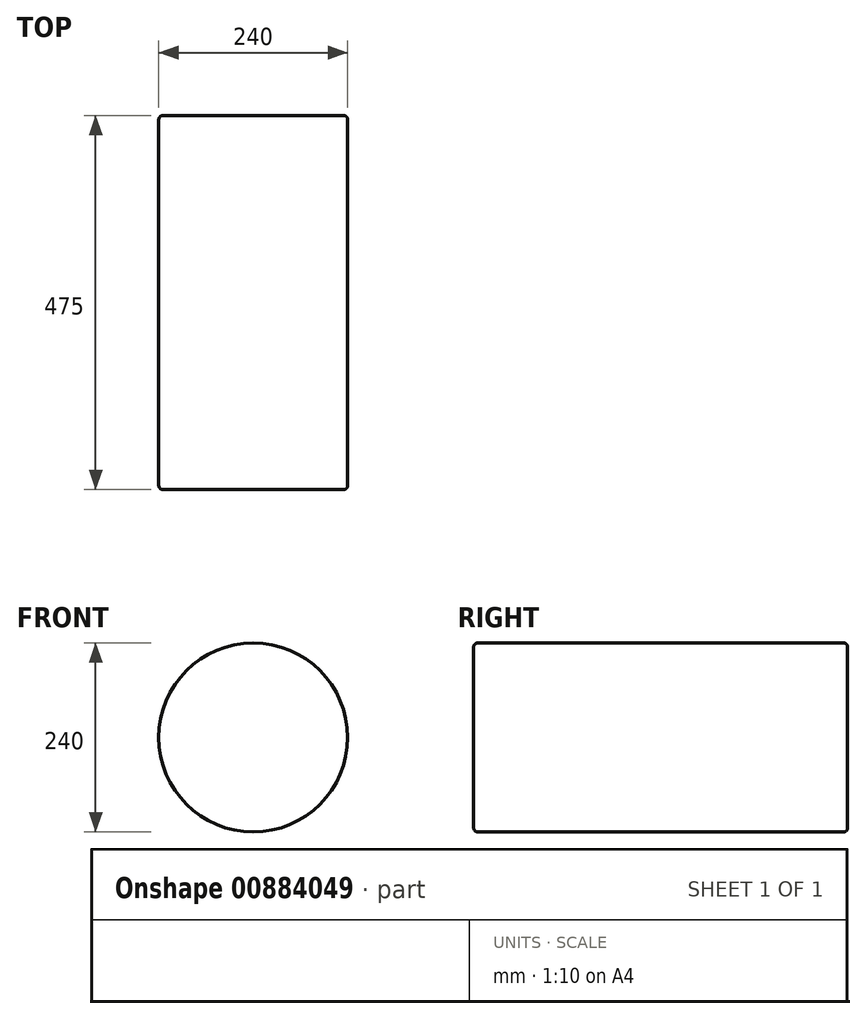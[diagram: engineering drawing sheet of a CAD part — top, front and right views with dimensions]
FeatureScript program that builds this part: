
annotation { "Feature Type Name" : "Feature", "Feature Type Description" : "" }
export const myFeature = defineFeature(function(context is Context, id is Id, definition is map)
    precondition{}
    {
        {
            var Q0;
            Q0=qCreatedBy(makeId("Front.planeOp"),FACE);
            var sketch = newSketch(context, id + "F0", { "sketchPlane" : qUnion([Q0])});
            skCircle(sketch, "E0", {"center": v(0, 0) * mm, "radius": 120 * mm});
            skCircle(sketch, "E1", {"center": v(0, 0) * mm, "radius": 62.5 * mm});
            skCircle(sketch, "E2", {"center": v(0, 0) * mm, "radius": 12.5 * mm});
            skSolve(sketch);
        }
        {
            var Q0;
            Q0=makeQuery(id+"F0.imprint","IMPRINT",FACE,{"disambiguationData":[TD([[makeQuery(id+"F0.imprint","IMPRINT",EDGE,{"derivedFrom":sQuery(id+"F0.wireOp",EDGE,"E2")}),1.0]])]});
            var Q1;
            Q1=makeQuery(id+"F0.imprint","IMPRINT",FACE,{"disambiguationData":[TD([[makeQuery(id+"F0.imprint","IMPRINT",EDGE,{"derivedFrom":sQuery(id+"F0.wireOp",EDGE,"E0")}),1.0]])]});
            var Q2;
            Q2=makeQuery(id+"F0.imprint","IMPRINT",FACE,{"disambiguationData":[TD([[makeQuery(id+"F0.imprint","IMPRINT",EDGE,{"derivedFrom":sQuery(id+"F0.wireOp",EDGE,"E1")}),1.0]])]});
            extrude(context, id + "F1", {"entities" : qUnion([Q0, Q1, Q2]), "oppositeDirection" : true, "depth" : 475 * mm, "offsetDistance" : 25.4 * mm});
        }
        {
            var Q0;
            Q0=makeQuery(id+"F1.opExtrude","CAP_EDGE",EDGE,{"disambiguationData":[OSD([sQuery(id+"F0.wireOp",EDGE,"E0")])],"isStart":true});
            var Q1;
            Q1=makeQuery(id+"F1.opExtrude","CAP_EDGE",EDGE,{"disambiguationData":[OSD([sQuery(id+"F0.wireOp",EDGE,"E0")])],"isStart":false});
            fillet(context, id + "F2", {"entities" : qUnion([Q0, Q1]), "radius" : 5.08 * mm, "tangentPropagation" : true, "allowEdgeOverflow" : false});
        }
    });
